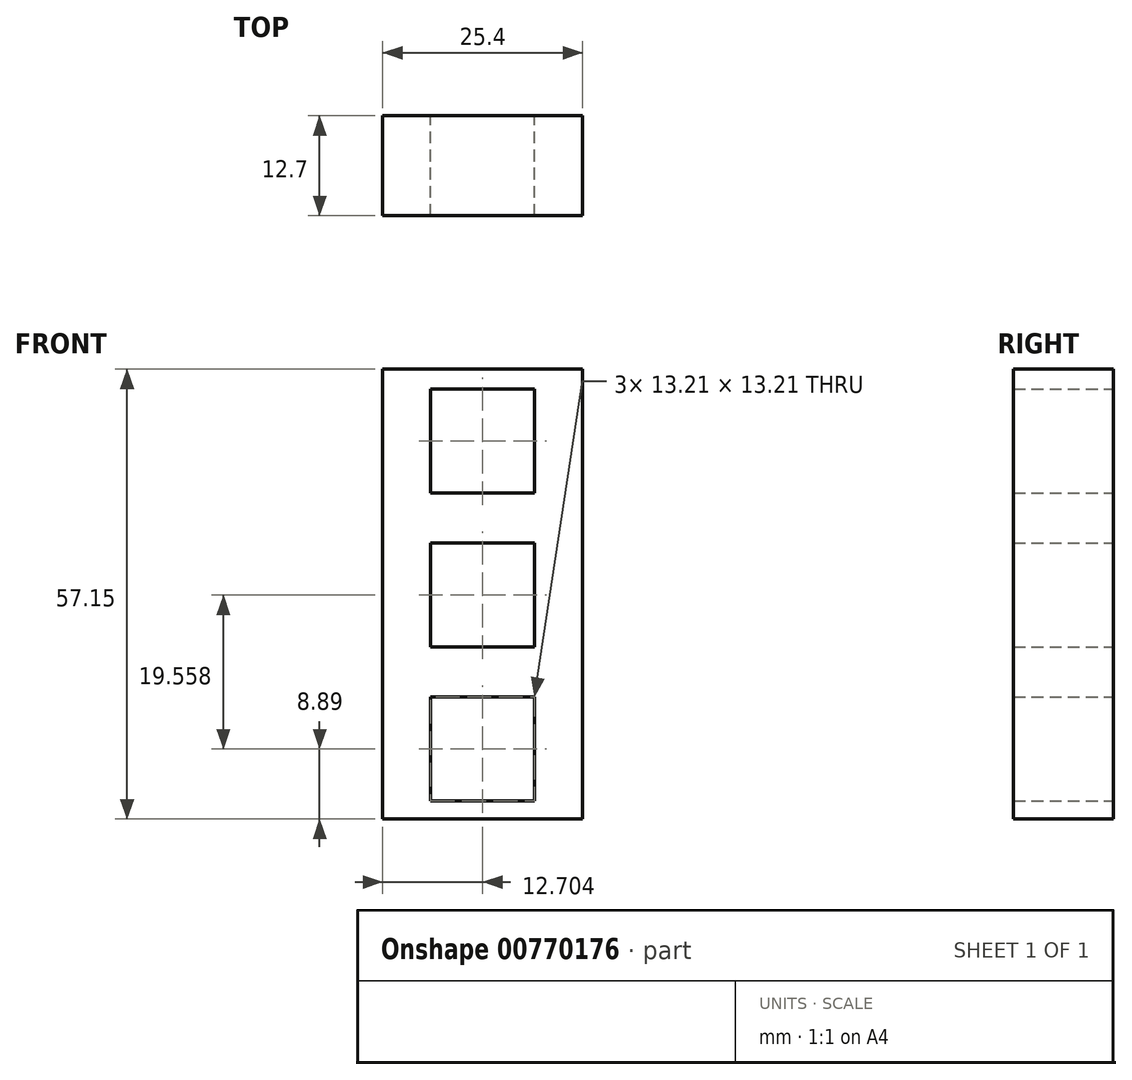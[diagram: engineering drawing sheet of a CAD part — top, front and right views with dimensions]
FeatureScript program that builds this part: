
annotation { "Feature Type Name" : "Feature", "Feature Type Description" : "" }
export const myFeature = defineFeature(function(context is Context, id is Id, definition is map)
    precondition{}
    {
        {
            var Q0;
            Q0=qCreatedBy(makeId("Front.planeOp"),FACE);
            var sketch = newSketch(context, id + "F0", { "sketchPlane" : qUnion([Q0])});
            skLineSegment(sketch, "E0.bottom", {"start": v(17.35, 2.54) * mm, "end": v(42.75, 2.54) * mm});
            skLineSegment(sketch, "E0.top", {"start": v(17.35, -54.61) * mm, "end": v(42.75, -54.61) * mm});
            skLineSegment(sketch, "E0.left", {"start": v(17.35, 2.54) * mm, "end": v(17.35, -54.61) * mm});
            skLineSegment(sketch, "E0.right", {"start": v(42.75, 2.54) * mm, "end": v(42.75, -54.6) * mm});
            skLineSegment(sketch, "E1.bottom", {"start": v(36.66, 0) * mm, "end": v(23.45, 0) * mm});
            skLineSegment(sketch, "E1.top", {"start": v(36.66, -13.2) * mm, "end": v(23.45, -13.2) * mm});
            skLineSegment(sketch, "E1.left", {"start": v(36.66, 0) * mm, "end": v(36.66, -13.2) * mm});
            skLineSegment(sketch, "E1.right", {"start": v(23.45, 0) * mm, "end": v(23.45, -13.2) * mm});
            skPoint(sketch, "E1.middle", {"position": v(30.05, -6.6) * mm});
            skLineSegment(sketch, "E2.bottom", {"start": v(23.45, -19.56) * mm, "end": v(36.66, -19.56) * mm});
            skLineSegment(sketch, "E2.top", {"start": v(23.45, -32.77) * mm, "end": v(36.66, -32.77) * mm});
            skLineSegment(sketch, "E2.left", {"start": v(23.45, -19.56) * mm, "end": v(23.45, -32.77) * mm});
            skLineSegment(sketch, "E2.right", {"start": v(36.66, -19.56) * mm, "end": v(36.66, -32.77) * mm});
            skPoint(sketch, "E2.middle", {"position": v(30.05, -26.16) * mm});
            skLineSegment(sketch, "E3.bottom", {"start": v(23.45, -52.32) * mm, "end": v(36.66, -52.32) * mm});
            skLineSegment(sketch, "E3.top", {"start": v(23.45, -39.12) * mm, "end": v(36.66, -39.12) * mm});
            skLineSegment(sketch, "E3.left", {"start": v(23.45, -52.32) * mm, "end": v(23.45, -39.12) * mm});
            skLineSegment(sketch, "E3.right", {"start": v(36.66, -52.32) * mm, "end": v(36.66, -39.12) * mm});
            skPoint(sketch, "E3.middle", {"position": v(30.05, -45.72) * mm});
            skSolve(sketch);
        }
        {
            var Q0;
            Q0=makeQuery(id+"F0.imprint","IMPRINT",FACE,{"disambiguationData":[TD([[makeQuery(id+"F0.imprint","IMPRINT",EDGE,{"derivedFrom":sQuery(id+"F0.wireOp",EDGE,"E0.bottom")}),-1.0]])]});
            extrude(context, id + "F1", {"entities" : qUnion([Q0]), "depth" : 12.7 * mm, "offsetDistance" : 25.4 * mm});
        }
    });
